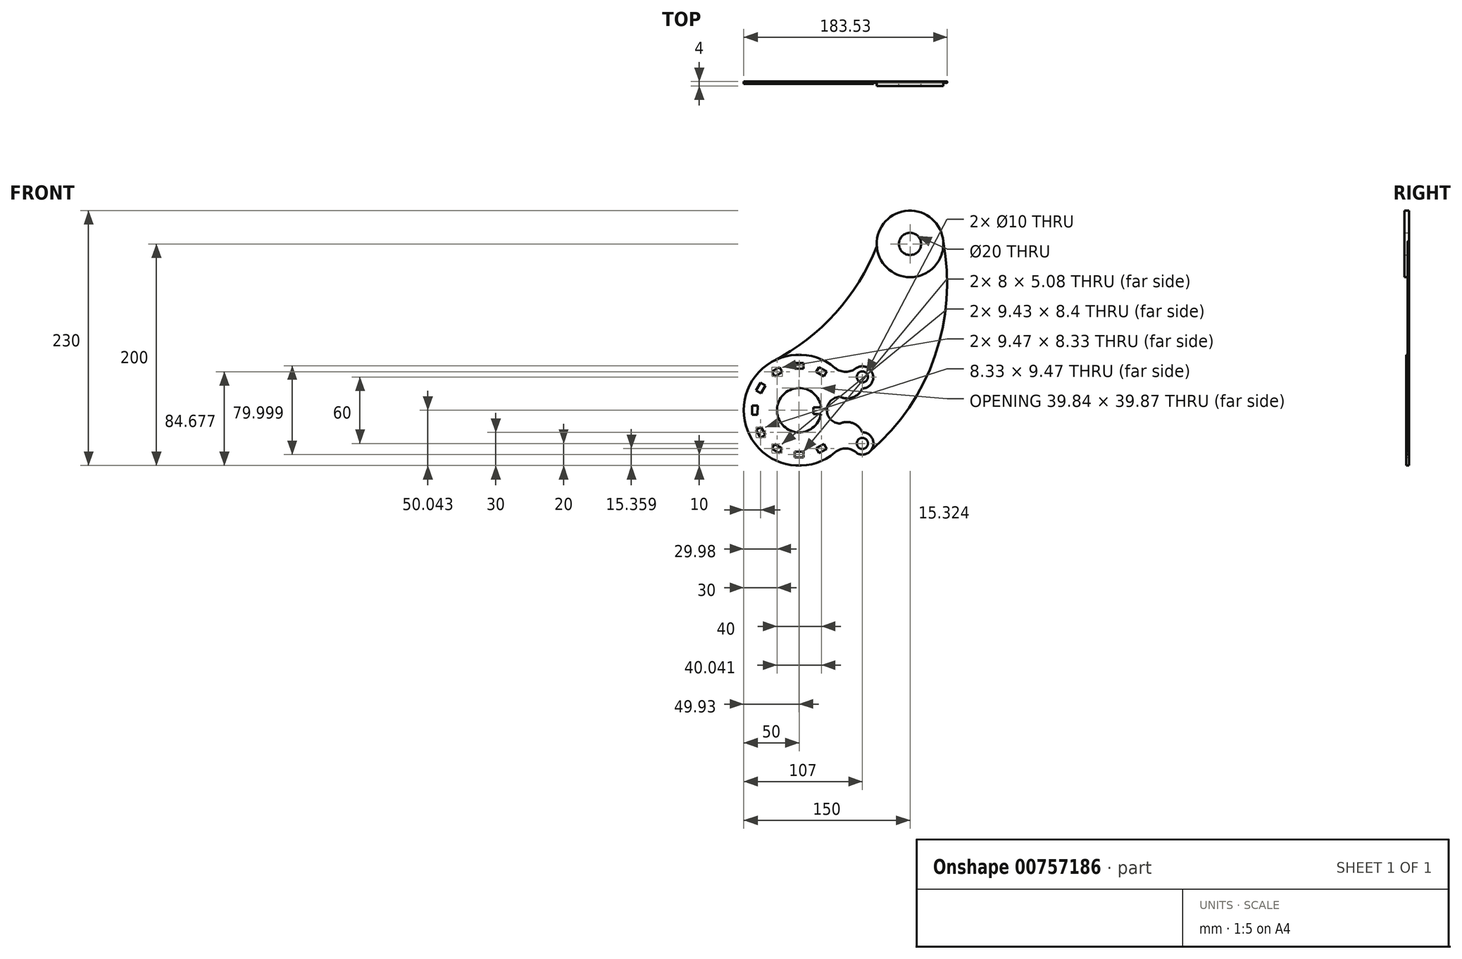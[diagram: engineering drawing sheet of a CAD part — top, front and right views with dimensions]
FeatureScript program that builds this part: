
annotation { "Feature Type Name" : "Feature", "Feature Type Description" : "" }
export const myFeature = defineFeature(function(context is Context, id is Id, definition is map)
    precondition{}
    {
        {
            var Q0;
            Q0=qCreatedBy(makeId("Front.planeOp"),FACE);
            var sketch = newSketch(context, id + "F0", { "sketchPlane" : qUnion([Q0])});
            skLineSegment(sketch, "E0", {"start": v(12.85, 2.43) * mm, "end": v(12.85, -3.57) * mm});
            skLineSegment(sketch, "E1", {"start": v(12.85, -3.57) * mm, "end": v(19.85, -3.57) * mm});
            skLineSegment(sketch, "E2", {"start": v(12.85, 2.43) * mm, "end": v(19.85, 2.43) * mm});
            skArc(sketch, "E3", {"start": v(19.85, 2.43) * mm, "mid": v(-20, 0.57) * mm, "end": v(19.68, -3.57) * mm});
            skArc(sketch, "E4.0", {"start": v(32.3, 38.16) * mm, "mid": v(-50, 0) * mm, "end": v(32.3, -38.16) * mm});
            skArc(sketch, "E5", {"start": v(57, -20) * mm, "mid": v(66.74, -32.27) * mm, "end": v(52.57, -38.97) * mm});
            skCircle(sketch, "E6", {"center": v(57, -30) * mm, "radius": 5 * mm});
            skCircle(sketch, "E7", {"center": v(57, 30) * mm, "radius": 5 * mm});
            skArc(sketch, "E8", {"start": v(37, 12) * mm, "mid": v(25, 0) * mm, "end": v(37, -12) * mm});
            skLineSegment(sketch, "E9", {"start": v(24.73, -34.84) * mm, "end": v(17.8, -38.84) * mm});
            skLineSegment(sketch, "E10", {"start": v(15.27, -34.44) * mm, "end": v(17.8, -38.84) * mm});
            skLineSegment(sketch, "E11", {"start": v(24.73, -34.84) * mm, "end": v(22.23, -30.51) * mm});
            skLineSegment(sketch, "E12", {"start": v(22.23, -30.51) * mm, "end": v(15.27, -34.44) * mm});
            skLineSegment(sketch, "E13.1.0", {"start": v(4, -42.54) * mm, "end": v(-4, -42.54) * mm});
            skLineSegment(sketch, "E13.1.1", {"start": v(4, -37.54) * mm, "end": v(-4, -37.46) * mm});
            skLineSegment(sketch, "E13.1.2", {"start": v(4, -42.54) * mm, "end": v(4, -37.54) * mm});
            skLineSegment(sketch, "E13.1.3", {"start": v(-4, -37.46) * mm, "end": v(-4, -42.54) * mm});
            skLineSegment(sketch, "E13.2.0", {"start": v(-17.8, -38.84) * mm, "end": v(-24.73, -34.84) * mm});
            skLineSegment(sketch, "E13.2.1", {"start": v(-15.3, -34.51) * mm, "end": v(-22.2, -30.44) * mm});
            skLineSegment(sketch, "E13.2.2", {"start": v(-17.8, -38.84) * mm, "end": v(-15.3, -34.51) * mm});
            skLineSegment(sketch, "E13.2.3", {"start": v(-22.2, -30.44) * mm, "end": v(-24.73, -34.84) * mm});
            skLineSegment(sketch, "E13.3.0", {"start": v(-34.84, -24.73) * mm, "end": v(-38.84, -17.8) * mm});
            skLineSegment(sketch, "E13.3.1", {"start": v(-30.51, -22.23) * mm, "end": v(-34.44, -15.27) * mm});
            skLineSegment(sketch, "E13.3.2", {"start": v(-34.84, -24.73) * mm, "end": v(-30.51, -22.23) * mm});
            skLineSegment(sketch, "E13.3.3", {"start": v(-34.44, -15.27) * mm, "end": v(-38.84, -17.8) * mm});
            skLineSegment(sketch, "E13.4.0", {"start": v(-42.54, -4) * mm, "end": v(-42.54, 4) * mm});
            skLineSegment(sketch, "E13.4.1", {"start": v(-37.54, -4) * mm, "end": v(-37.46, 4) * mm});
            skLineSegment(sketch, "E13.4.2", {"start": v(-42.54, -4) * mm, "end": v(-37.54, -4) * mm});
            skLineSegment(sketch, "E13.4.3", {"start": v(-37.46, 4) * mm, "end": v(-42.54, 4) * mm});
            skLineSegment(sketch, "E13.5.0", {"start": v(-38.84, 17.8) * mm, "end": v(-34.84, 24.73) * mm});
            skLineSegment(sketch, "E13.5.1", {"start": v(-34.51, 15.3) * mm, "end": v(-30.44, 22.2) * mm});
            skLineSegment(sketch, "E13.5.2", {"start": v(-38.84, 17.8) * mm, "end": v(-34.51, 15.3) * mm});
            skLineSegment(sketch, "E13.5.3", {"start": v(-30.44, 22.2) * mm, "end": v(-34.84, 24.73) * mm});
            skLineSegment(sketch, "E13.6.0", {"start": v(-24.73, 34.84) * mm, "end": v(-17.8, 38.84) * mm});
            skLineSegment(sketch, "E13.6.1", {"start": v(-22.23, 30.51) * mm, "end": v(-15.27, 34.44) * mm});
            skLineSegment(sketch, "E13.6.2", {"start": v(-24.73, 34.84) * mm, "end": v(-22.23, 30.51) * mm});
            skLineSegment(sketch, "E13.6.3", {"start": v(-15.27, 34.44) * mm, "end": v(-17.8, 38.84) * mm});
            skLineSegment(sketch, "E13.7.0", {"start": v(-4, 42.54) * mm, "end": v(4, 42.54) * mm});
            skLineSegment(sketch, "E13.7.1", {"start": v(-4, 37.54) * mm, "end": v(4, 37.46) * mm});
            skLineSegment(sketch, "E13.7.2", {"start": v(-4, 42.54) * mm, "end": v(-4, 37.54) * mm});
            skLineSegment(sketch, "E13.7.3", {"start": v(4, 37.46) * mm, "end": v(4, 42.54) * mm});
            skLineSegment(sketch, "E13.8.0", {"start": v(17.8, 38.84) * mm, "end": v(24.73, 34.84) * mm});
            skLineSegment(sketch, "E13.8.1", {"start": v(15.3, 34.51) * mm, "end": v(22.2, 30.44) * mm});
            skLineSegment(sketch, "E13.8.2", {"start": v(17.8, 38.84) * mm, "end": v(15.3, 34.51) * mm});
            skLineSegment(sketch, "E13.8.3", {"start": v(22.2, 30.44) * mm, "end": v(24.73, 34.84) * mm});
            skArc(sketch, "E14", {"start": v(52.57, -38.97) * mm, "mid": v(42.6, -34.62) * mm, "end": v(32.3, -38.16) * mm});
            skArc(sketch, "E15", {"start": v(32.3, 38.16) * mm, "mid": v(42, 34.6) * mm, "end": v(51.7, 38.16) * mm});
            skArc(sketch, "E16", {"start": v(37, 12) * mm, "mid": v(48.59, 11.6) * mm, "end": v(57, 19.58) * mm});
            skArc(sketch, "E17", {"start": v(57, -20) * mm, "mid": v(48.7, -11.77) * mm, "end": v(37, -12) * mm});
            skCircle(sketch, "E18", {"center": v(100, 150) * mm, "radius": 30 * mm});
            skCircle(sketch, "E19", {"center": v(100, 150) * mm, "radius": 10 * mm});
            skArc(sketch, "E20", {"start": v(57, 19.58) * mm, "mid": v(66.45, 32.33) * mm, "end": v(51.7, 38.16) * mm});
            skArc(sketch, "E21", {"start": v(64.02, -37.12) * mm, "mid": v(122.43, 48.75) * mm, "end": v(129.9, 152.34) * mm});
            skArc(sketch, "E22", {"start": v(-23.14, 44.32) * mm, "mid": v(32.75, 87.6) * mm, "end": v(70.1, 147.62) * mm});
            skSolve(sketch);
        }
        {
            var Q0;
            {var subQ11=sQuery(id+"F0.wireOp",EDGE,"E0");Q0=makeQuery(id+"F0.imprint","IMPRINT",FACE,{"disambiguationData":[TD([[makeQuery(id+"F0.imprint","IMPRINT",EDGE,{"derivedFrom":subQ11}),1.0]])]});}
            extrude(context, id + "F1", {"entities" : qUnion([Q0]), "depth" : 2.3 * mm, "offsetDistance" : 25 * mm});
        }
        {
            var Q0;
            Q0=makeQuery(id+"F0.imprint","IMPRINT",FACE,{"disambiguationData":[TD([[makeQuery(id+"F0.imprint","IMPRINT",EDGE,{"derivedFrom":sQuery(id+"F0.wireOp",EDGE,"E8")}),1.0]])]});
            extrude(context, id + "F2", {"entities" : qUnion([Q0]), "operationType" : NewBodyOperationType.ADD, "depth" : 1.2 * mm, "offsetDistance" : 25 * mm});
        }
        {
            var Q0;
            Q0=makeQuery(id+"F0.imprint","IMPRINT",FACE,{"disambiguationData":[TD([[makeQuery(id+"F0.imprint","IMPRINT",EDGE,{"derivedFrom":sQuery(id+"F0.wireOp",EDGE,"E19")}),-1.0]])]});
            extrude(context, id + "F3", {"entities" : qUnion([Q0]), "operationType" : NewBodyOperationType.ADD, "depth" : 4 * mm, "offsetDistance" : 25 * mm});
        }
        {
            var Q0;
            Q0=makeQuery(id+"F2.opExtrude","CAP_EDGE",EDGE,{"disambiguationData":[OSD([sQuery(id+"F0.wireOp",EDGE,"E21")])],"isStart":false});
            fillet(context, id + "F4", {"entities" : qUnion([Q0]), "radius" : .25 * mm, "tangentPropagation" : true, "allowEdgeOverflow" : false});
        }
        {
            var Q0;
            Q0=makeQuery(id+"F2.opExtrude","CAP_EDGE",EDGE,{"disambiguationData":[OSD([sQuery(id+"F0.wireOp",EDGE,"E22")])],"isStart":false});
            fillet(context, id + "F5", {"entities" : qUnion([Q0]), "radius" : .25 * mm, "tangentPropagation" : true, "allowEdgeOverflow" : false});
        }
    });
